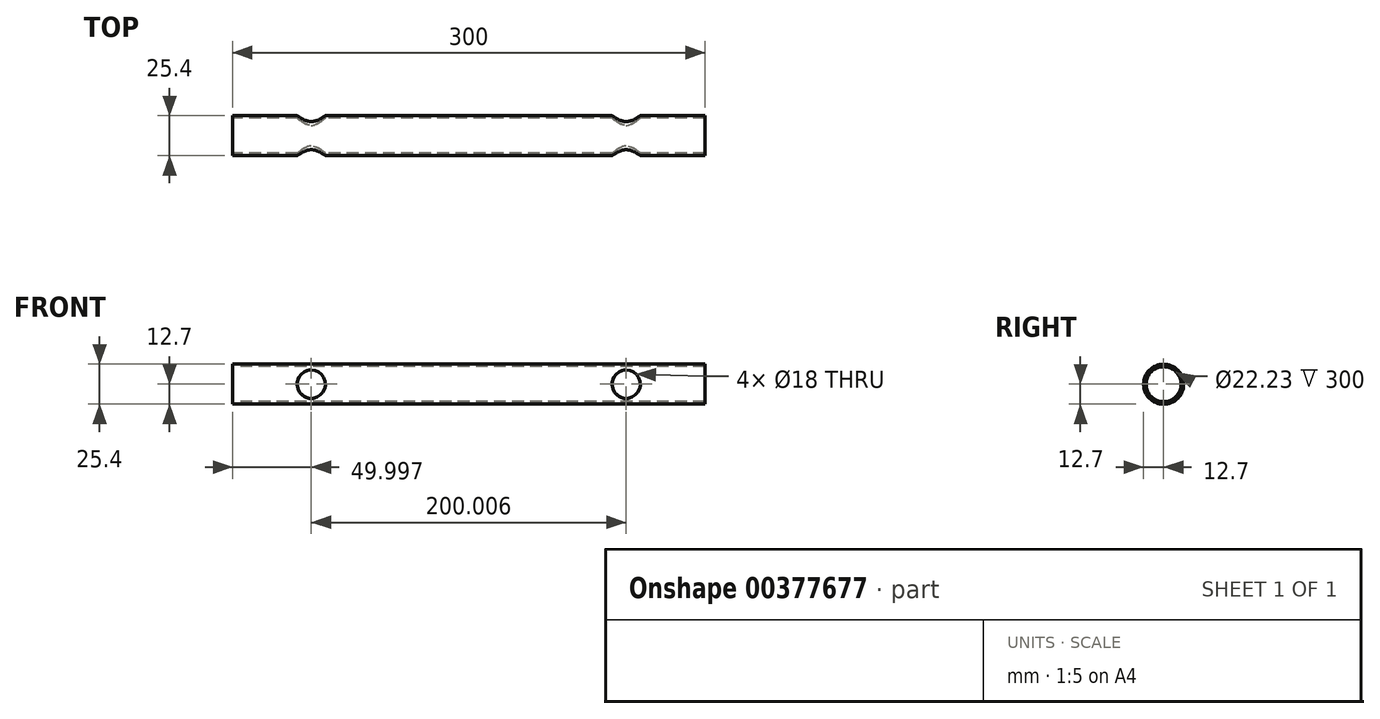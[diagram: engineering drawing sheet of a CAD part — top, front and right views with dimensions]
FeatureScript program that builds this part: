
annotation { "Feature Type Name" : "Feature", "Feature Type Description" : "" }
export const myFeature = defineFeature(function(context is Context, id is Id, definition is map)
    precondition{}
    {
        {
            var Q0;
            Q0=qCreatedBy(makeId("Right.planeOp"),FACE);
            var sketch = newSketch(context, id + "F0", { "sketchPlane" : qUnion([Q0])});
            skCircle(sketch, "E0", {"center": v(0, 0) * mm, "radius": 11.11 * mm});
            skCircle(sketch, "E1", {"center": v(0, 0) * mm, "radius": 12.7 * mm});
            skSolve(sketch);
        }
        {
            var Q0;
            Q0 = qSketchRegion(id + "F0", true);
            extrude(context, id + "F1", {"entities" : qUnion([Q0]), "depth" : 300 * mm, "symmetric" : true});
        }
        {
            var Q0;
            Q0=qCreatedBy(makeId("Front.planeOp"),FACE);
            var sketch = newSketch(context, id + "F2", { "sketchPlane" : qUnion([Q0])});
            skLineSegment(sketch, "E2", {"start": v(-142.5, 0) * mm, "end": v(142.9, 0) * mm, "construction": true});
            skCircle(sketch, "E3", {"center": v(-100, 0) * mm, "radius": 9 * mm});
            skLineSegment(sketch, "E4", {"start": v(0, 0) * mm, "end": v(0, 28.42) * mm, "construction": true});
            skCircle(sketch, "E5.MirrorC", {"center": v(100, 0) * mm, "radius": 9 * mm});
            skSolve(sketch);
        }
        {
            var Q0;
            Q0 = qSketchRegion(id + "F2", true);
            extrude(context, id + "F3", {"entities" : qUnion([Q0]), "operationType" : NewBodyOperationType.REMOVE, "depth" : 30 * mm, "symmetric" : true});
        }
    });
